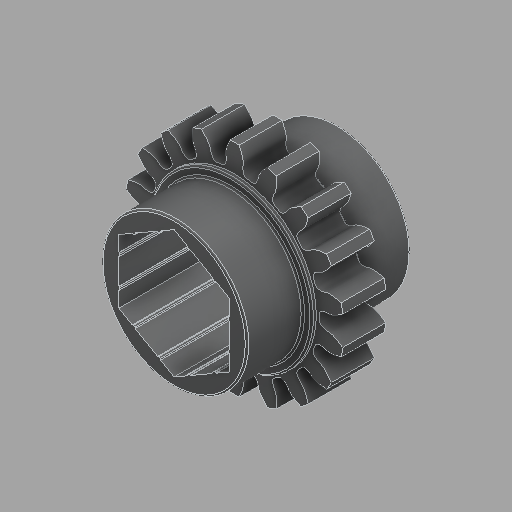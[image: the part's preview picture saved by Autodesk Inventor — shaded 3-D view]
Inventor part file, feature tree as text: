
AUTODESK INVENTOR PART (.ipt)
format: ipt  version: 2024.2 (Build 282272000, 272)  size: 410,112 bytes
history: native  units: in
note: dims shown in document units (in); Inventor stores cm internally (conversion verified against a paired STEP export)
features: fillet x1
ambient origin geometry x8: Origin, YZ Plane, XZ Plane, XY Plane, X Axis, Y Axis, Z Axis, Center Point
bodies: Solid1 (feature_tree)
feature tree (1):
  fillet  "Fillet1"  [1 undecoded]
note: 1 required parameter value undecoded (feature->parameter linkage not recoverable at this tier; creation-order binding heuristic only, values carry confidence <= 0.55)
